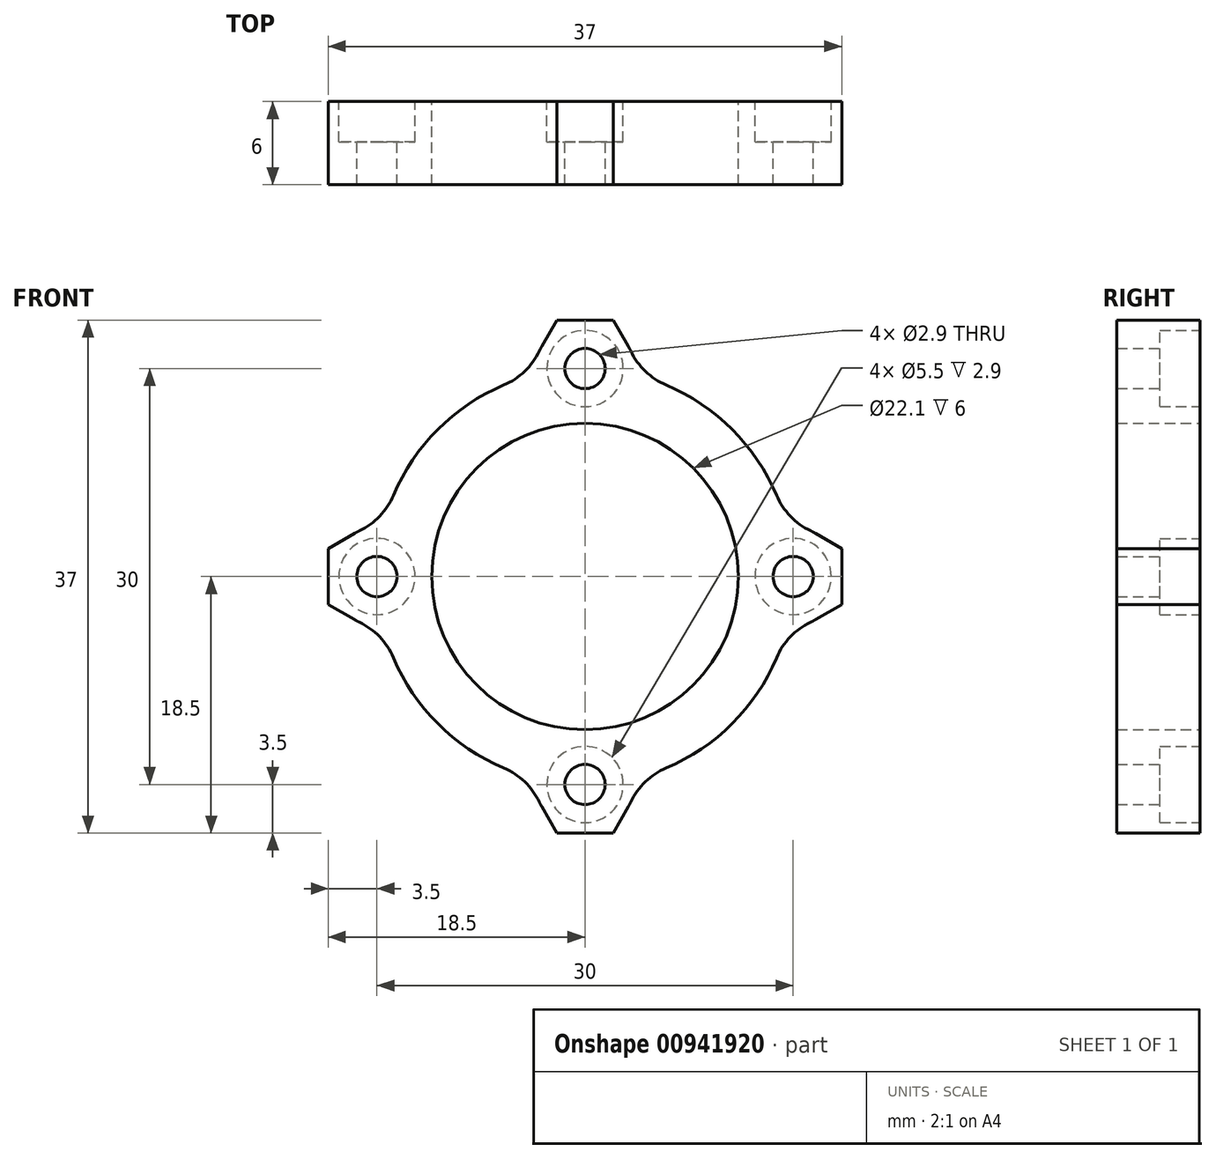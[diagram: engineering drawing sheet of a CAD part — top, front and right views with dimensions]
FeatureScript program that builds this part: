
annotation { "Feature Type Name" : "Feature", "Feature Type Description" : "" }
export const myFeature = defineFeature(function(context is Context, id is Id, definition is map)
    precondition{}
    {
        {
            var Q0;
            Q0=qCreatedBy(makeId("Front.planeOp"),FACE);
            var sketch = newSketch(context, id + "F0", { "sketchPlane" : qUnion([Q0])});
            skCircle(sketch, "E0", {"center": v(0, 0) * mm, "radius": 11.05 * mm});
            skCircle(sketch, "E1", {"center": v(0, 0) * mm, "radius": 15 * mm});
            skPoint(sketch, "E2", {"position": v(0, 15) * mm});
            skCircle(sketch, "E3.cCircle", {"center": v(0, 15) * mm, "radius": 3.5 * mm, "construction": true});
            skLineSegment(sketch, "E3.0", {"start": v(-2.02, 18.5) * mm, "end": v(2.02, 18.5) * mm});
            skLineSegment(sketch, "E3.1", {"start": v(2.02, 18.5) * mm, "end": v(4.04, 15) * mm});
            skLineSegment(sketch, "E3.2", {"start": v(4.04, 15) * mm, "end": v(2.02, 11.5) * mm});
            skLineSegment(sketch, "E3.3", {"start": v(2.02, 11.5) * mm, "end": v(-2.02, 11.5) * mm});
            skLineSegment(sketch, "E3.4", {"start": v(-2.02, 11.5) * mm, "end": v(-4.04, 15) * mm});
            skLineSegment(sketch, "E3.5", {"start": v(-4.04, 15) * mm, "end": v(-2.02, 18.5) * mm});
            skPoint(sketch, "E3.0.midPoint", {"position": v(0, 18.5) * mm});
            skPoint(sketch, "E4", {"position": v(-15, 0) * mm});
            skPoint(sketch, "E5", {"position": v(15, 0) * mm});
            skLineSegment(sketch, "E6", {"start": v(-15, 0) * mm, "end": v(15, 0) * mm});
            skLineSegment(sketch, "E7.MirrorCS", {"start": v(-2.02, -18.5) * mm, "end": v(2.02, -18.5) * mm});
            skLineSegment(sketch, "E8.MirrorCS", {"start": v(-4.04, -15) * mm, "end": v(-2.02, -18.5) * mm});
            skLineSegment(sketch, "E9.MirrorCS", {"start": v(4.04, -15) * mm, "end": v(2.02, -11.5) * mm});
            skLineSegment(sketch, "E10.MirrorCS", {"start": v(-2.02, -11.5) * mm, "end": v(-4.04, -15) * mm});
            skLineSegment(sketch, "E11.MirrorCS", {"start": v(2.02, -11.5) * mm, "end": v(-2.02, -11.5) * mm});
            skLineSegment(sketch, "E12.MirrorCS", {"start": v(2.02, -18.5) * mm, "end": v(4.04, -15) * mm});
            skLineSegment(sketch, "E13", {"start": v(0, 0) * mm, "end": v(10.6, 10.6) * mm});
            skLineSegment(sketch, "E14.MirrorCS", {"start": v(15, 4.04) * mm, "end": v(11.5, 2.02) * mm});
            skLineSegment(sketch, "E15.MirrorCS", {"start": v(11.5, 2.02) * mm, "end": v(11.5, -2.02) * mm});
            skLineSegment(sketch, "E16.MirrorCS", {"start": v(11.5, -2.02) * mm, "end": v(15, -4.04) * mm});
            skLineSegment(sketch, "E17.MirrorCS", {"start": v(15, -4.04) * mm, "end": v(18.5, -2.02) * mm});
            skLineSegment(sketch, "E18.MirrorCS", {"start": v(18.5, -2.02) * mm, "end": v(18.5, 2.02) * mm});
            skLineSegment(sketch, "E19.MirrorCS", {"start": v(18.5, 2.02) * mm, "end": v(15, 4.04) * mm});
            skLineSegment(sketch, "E20", {"start": v(0, 15) * mm, "end": v(0, 0) * mm});
            skLineSegment(sketch, "E21.MirrorCS", {"start": v(-15, 4.04) * mm, "end": v(-11.5, 2.02) * mm});
            skLineSegment(sketch, "E22.MirrorCS", {"start": v(-11.5, 2.02) * mm, "end": v(-11.5, -2.02) * mm});
            skLineSegment(sketch, "E23.MirrorCS", {"start": v(-11.5, -2.02) * mm, "end": v(-15, -4.04) * mm});
            skLineSegment(sketch, "E24.MirrorCS", {"start": v(-15, -4.04) * mm, "end": v(-18.5, -2.02) * mm});
            skLineSegment(sketch, "E25.MirrorCS", {"start": v(-18.5, -2.02) * mm, "end": v(-18.5, 2.02) * mm});
            skLineSegment(sketch, "E26.MirrorCS", {"start": v(-18.5, 2.02) * mm, "end": v(-15, 4.04) * mm});
            skCircle(sketch, "E27", {"center": v(0, 15) * mm, "radius": 1.45 * mm});
            skCircle(sketch, "E28", {"center": v(15, 0) * mm, "radius": 1.45 * mm});
            skCircle(sketch, "E29", {"center": v(-15, 0) * mm, "radius": 1.45 * mm});
            skCircle(sketch, "E30", {"center": v(0, -15) * mm, "radius": 1.45 * mm});
            skSolve(sketch);
        }
        {
            var Q0;
            Q0 = qSketchRegion(id + "F0", true);
            extrude(context, id + "F1", {"entities" : qUnion([Q0]), "depth" : 6 * mm, "offsetDistance" : 25 * mm});
        }
        {
            var Q0;
            Q0=makeQuery(id+"F1.opExtrude","SWEPT_EDGE",EDGE,{"disambiguationData":[OSD([sQuery(id+"F0.wireOp",EDGE,"E3.4"),sQuery(id+"F0.wireOp",EDGE,"E3.5")])]});
            fillet(context, id + "F2", {"entities" : qUnion([Q0]), "radius" : 5 * mm, "tangentPropagation" : true, "allowEdgeOverflow" : false});
        }
        {
            var Q0;
            {var subQ0=sQuery(id+"F0.wireOp",EDGE,"E3.4");var subQ1=sQuery(id+"F0.wireOp",EDGE,"E1");Q0=makeQuery(id+"F2.opFillet","BLEND_EDGE",EDGE,{"blendedFrom":[makeQuery(id+"F1.opExtrude","SWEPT_EDGE",EDGE,{"disambiguationData":[OSD([subQ0,sQuery(id+"F0.wireOp",EDGE,"E3.5")])]}),makeQuery(id+"F1.opExtrude","SWEPT_FACE",FACE,{"disambiguationData":[OSD([subQ1]),TDD([makeQuery(id+"F0.imprint","IMPRINT",EDGE,{"disambiguationData":[TD([[makeQuery(id+"F0.imprint","INTERSECT",VERTEX,{"derivedFrom":[subQ1,subQ0]}),-1.0]])],"derivedFrom":subQ1})])]})],"blendedInto":[makeQuery(id+"F1.opExtrude","SWEPT_FACE",FACE,{"disambiguationData":[OSD([subQ1]),TDD([makeQuery(id+"F0.imprint","IMPRINT",EDGE,{"disambiguationData":[TD([[makeQuery(id+"F0.imprint","INTERSECT",VERTEX,{"derivedFrom":[subQ1,subQ0]}),-1.0]])],"derivedFrom":subQ1})])]})]});}
            fillet(context, id + "F3", {"entities" : qUnion([Q0]), "radius" : 5 * mm, "tangentPropagation" : true, "allowEdgeOverflow" : false});
        }
        {
            var Q0;
            Q0=makeQuery(id+"F1.opExtrude","SWEPT_EDGE",EDGE,{"disambiguationData":[OSD([sQuery(id+"F0.wireOp",EDGE,"E3.1"),sQuery(id+"F0.wireOp",EDGE,"E3.2")])]});
            fillet(context, id + "F4", {"entities" : qUnion([Q0]), "radius" : 5 * mm, "tangentPropagation" : true, "allowEdgeOverflow" : false});
        }
        {
            var Q0;
            {var subQ0=sQuery(id+"F0.wireOp",EDGE,"E1");var subQ1=makeQuery(id+"F0.imprint","INTERSECT",VERTEX,{"derivedFrom":[subQ0,sQuery(id+"F0.wireOp",EDGE,"E13")]});var subQ2=sQuery(id+"F0.wireOp",EDGE,"E3.2");Q0=makeQuery(id+"F4.opFillet","BLEND_EDGE",EDGE,{"blendedFrom":[makeQuery(id+"F1.opExtrude","SWEPT_EDGE",EDGE,{"disambiguationData":[OSD([sQuery(id+"F0.wireOp",EDGE,"E3.1"),subQ2])]}),makeQuery(id+"F1.opExtrude","SWEPT_FACE",FACE,{"disambiguationData":[OSD([subQ0]),TDD([makeQuery(id+"F0.imprint","IMPRINT",EDGE,{"disambiguationData":[TD([[subQ1,1.0]])],"derivedFrom":subQ0}),makeQuery(id+"F0.imprint","IMPRINT",EDGE,{"disambiguationData":[TD([[subQ1,-1.0]])],"derivedFrom":subQ0})])]})],"blendedInto":[makeQuery(id+"F1.opExtrude","SWEPT_FACE",FACE,{"disambiguationData":[OSD([subQ0]),TDD([makeQuery(id+"F0.imprint","IMPRINT",EDGE,{"disambiguationData":[TD([[subQ1,1.0]])],"derivedFrom":subQ0}),makeQuery(id+"F0.imprint","IMPRINT",EDGE,{"disambiguationData":[TD([[subQ1,-1.0]])],"derivedFrom":subQ0})])]})]});}
            fillet(context, id + "F5", {"entities" : qUnion([Q0]), "radius" : 5 * mm, "tangentPropagation" : true, "allowEdgeOverflow" : false});
        }
        {
            var Q0;
            Q0=makeQuery(id+"F1.opExtrude","SWEPT_EDGE",EDGE,{"disambiguationData":[OSD([sQuery(id+"F0.wireOp",EDGE,"E14.MirrorCS"),sQuery(id+"F0.wireOp",EDGE,"E19.MirrorCS")])]});
            var Q1;
            Q1=makeQuery(id+"F1.opExtrude","SWEPT_EDGE",EDGE,{"disambiguationData":[OSD([sQuery(id+"F0.wireOp",EDGE,"E16.MirrorCS"),sQuery(id+"F0.wireOp",EDGE,"E17.MirrorCS")])]});
            fillet(context, id + "F6", {"entities" : qUnion([Q0, Q1]), "radius" : 5 * mm, "tangentPropagation" : true, "allowEdgeOverflow" : false});
        }
        {
            var Q0;
            {var subQ0=sQuery(id+"F0.wireOp",EDGE,"E1");var subQ1=makeQuery(id+"F0.imprint","INTERSECT",VERTEX,{"derivedFrom":[subQ0,sQuery(id+"F0.wireOp",EDGE,"E13")]});var subQ2=sQuery(id+"F0.wireOp",EDGE,"E14.MirrorCS");Q0=makeQuery(id+"F6.opFillet","BLEND_EDGE",EDGE,{"blendedFrom":[makeQuery(id+"F1.opExtrude","SWEPT_EDGE",EDGE,{"disambiguationData":[OSD([subQ2,sQuery(id+"F0.wireOp",EDGE,"E19.MirrorCS")])]}),makeQuery(id+"F1.opExtrude","SWEPT_FACE",FACE,{"disambiguationData":[OSD([subQ0]),TDD([makeQuery(id+"F0.imprint","IMPRINT",EDGE,{"disambiguationData":[TD([[subQ1,1.0]])],"derivedFrom":subQ0}),makeQuery(id+"F0.imprint","IMPRINT",EDGE,{"disambiguationData":[TD([[subQ1,-1.0]])],"derivedFrom":subQ0})])]})],"blendedInto":[makeQuery(id+"F1.opExtrude","SWEPT_FACE",FACE,{"disambiguationData":[OSD([subQ0]),TDD([makeQuery(id+"F0.imprint","IMPRINT",EDGE,{"disambiguationData":[TD([[subQ1,1.0]])],"derivedFrom":subQ0}),makeQuery(id+"F0.imprint","IMPRINT",EDGE,{"disambiguationData":[TD([[subQ1,-1.0]])],"derivedFrom":subQ0})])]})]});}
            var Q1;
            {var subQ0=sQuery(id+"F0.wireOp",EDGE,"E1");var subQ1=sQuery(id+"F0.wireOp",EDGE,"E16.MirrorCS");Q1=makeQuery(id+"F6.opFillet","BLEND_EDGE",EDGE,{"blendedFrom":[makeQuery(id+"F1.opExtrude","SWEPT_EDGE",EDGE,{"disambiguationData":[OSD([subQ1,sQuery(id+"F0.wireOp",EDGE,"E17.MirrorCS")])]}),makeQuery(id+"F1.opExtrude","SWEPT_FACE",FACE,{"disambiguationData":[OSD([subQ0]),TDD([makeQuery(id+"F0.imprint","IMPRINT",EDGE,{"disambiguationData":[TD([[makeQuery(id+"F0.imprint","INTERSECT",VERTEX,{"derivedFrom":[subQ0,sQuery(id+"F0.wireOp",EDGE,"E9.MirrorCS")]}),-1.0]])],"derivedFrom":subQ0})])]})],"blendedInto":[makeQuery(id+"F1.opExtrude","SWEPT_FACE",FACE,{"disambiguationData":[OSD([subQ0]),TDD([makeQuery(id+"F0.imprint","IMPRINT",EDGE,{"disambiguationData":[TD([[makeQuery(id+"F0.imprint","INTERSECT",VERTEX,{"derivedFrom":[subQ0,sQuery(id+"F0.wireOp",EDGE,"E9.MirrorCS")]}),-1.0]])],"derivedFrom":subQ0})])]})]});}
            fillet(context, id + "F7", {"entities" : qUnion([Q0, Q1]), "radius" : 5 * mm, "tangentPropagation" : true, "allowEdgeOverflow" : false});
        }
        {
            var Q0;
            Q0=makeQuery(id+"F1.opExtrude","SWEPT_EDGE",EDGE,{"disambiguationData":[OSD([sQuery(id+"F0.wireOp",EDGE,"E8.MirrorCS"),sQuery(id+"F0.wireOp",EDGE,"E10.MirrorCS")])]});
            fillet(context, id + "F8", {"entities" : qUnion([Q0]), "radius" : 5 * mm, "tangentPropagation" : true, "allowEdgeOverflow" : false});
        }
        {
            var Q0;
            {var subQ0=sQuery(id+"F0.wireOp",EDGE,"E1");var subQ1=sQuery(id+"F0.wireOp",EDGE,"E10.MirrorCS");Q0=makeQuery(id+"F8.opFillet","BLEND_EDGE",EDGE,{"blendedFrom":[makeQuery(id+"F1.opExtrude","SWEPT_EDGE",EDGE,{"disambiguationData":[OSD([sQuery(id+"F0.wireOp",EDGE,"E8.MirrorCS"),subQ1])]}),makeQuery(id+"F1.opExtrude","SWEPT_FACE",FACE,{"disambiguationData":[OSD([subQ0]),TDD([makeQuery(id+"F0.imprint","IMPRINT",EDGE,{"disambiguationData":[TD([[makeQuery(id+"F0.imprint","INTERSECT",VERTEX,{"derivedFrom":[subQ0,sQuery(id+"F0.wireOp",EDGE,"E23.MirrorCS")]}),-1.0]])],"derivedFrom":subQ0})])]})],"blendedInto":[makeQuery(id+"F1.opExtrude","SWEPT_FACE",FACE,{"disambiguationData":[OSD([subQ0]),TDD([makeQuery(id+"F0.imprint","IMPRINT",EDGE,{"disambiguationData":[TD([[makeQuery(id+"F0.imprint","INTERSECT",VERTEX,{"derivedFrom":[subQ0,sQuery(id+"F0.wireOp",EDGE,"E23.MirrorCS")]}),-1.0]])],"derivedFrom":subQ0})])]})]});}
            fillet(context, id + "F9", {"entities" : qUnion([Q0]), "radius" : 5 * mm, "tangentPropagation" : true, "allowEdgeOverflow" : false});
        }
        {
            var Q0;
            Q0=makeQuery(id+"F1.opExtrude","SWEPT_EDGE",EDGE,{"disambiguationData":[OSD([sQuery(id+"F0.wireOp",EDGE,"E9.MirrorCS"),sQuery(id+"F0.wireOp",EDGE,"E12.MirrorCS")])]});
            fillet(context, id + "F10", {"entities" : qUnion([Q0]), "radius" : 5 * mm, "tangentPropagation" : true, "allowEdgeOverflow" : false});
        }
        {
            var Q0;
            {var subQ0=sQuery(id+"F0.wireOp",EDGE,"E9.MirrorCS");var subQ1=sQuery(id+"F0.wireOp",EDGE,"E1");Q0=makeQuery(id+"F10.opFillet","BLEND_EDGE",EDGE,{"blendedFrom":[makeQuery(id+"F1.opExtrude","SWEPT_EDGE",EDGE,{"disambiguationData":[OSD([subQ0,sQuery(id+"F0.wireOp",EDGE,"E12.MirrorCS")])]}),makeQuery(id+"F1.opExtrude","SWEPT_FACE",FACE,{"disambiguationData":[OSD([subQ1]),TDD([makeQuery(id+"F0.imprint","IMPRINT",EDGE,{"disambiguationData":[TD([[makeQuery(id+"F0.imprint","INTERSECT",VERTEX,{"derivedFrom":[subQ1,subQ0]}),-1.0]])],"derivedFrom":subQ1})])]})],"blendedInto":[makeQuery(id+"F1.opExtrude","SWEPT_FACE",FACE,{"disambiguationData":[OSD([subQ1]),TDD([makeQuery(id+"F0.imprint","IMPRINT",EDGE,{"disambiguationData":[TD([[makeQuery(id+"F0.imprint","INTERSECT",VERTEX,{"derivedFrom":[subQ1,subQ0]}),-1.0]])],"derivedFrom":subQ1})])]})]});}
            fillet(context, id + "F11", {"entities" : qUnion([Q0]), "radius" : 5 * mm, "tangentPropagation" : true, "allowEdgeOverflow" : false});
        }
        {
            var Q0;
            Q0=makeQuery(id+"F1.opExtrude","SWEPT_EDGE",EDGE,{"disambiguationData":[OSD([sQuery(id+"F0.wireOp",EDGE,"E23.MirrorCS"),sQuery(id+"F0.wireOp",EDGE,"E24.MirrorCS")])]});
            var Q1;
            Q1=makeQuery(id+"F1.opExtrude","SWEPT_EDGE",EDGE,{"disambiguationData":[OSD([sQuery(id+"F0.wireOp",EDGE,"E21.MirrorCS"),sQuery(id+"F0.wireOp",EDGE,"E26.MirrorCS")])]});
            fillet(context, id + "F12", {"entities" : qUnion([Q0, Q1]), "radius" : 5 * mm, "tangentPropagation" : true, "allowEdgeOverflow" : false});
        }
        {
            var Q0;
            {var subQ0=sQuery(id+"F0.wireOp",EDGE,"E1");var subQ1=sQuery(id+"F0.wireOp",EDGE,"E21.MirrorCS");Q0=makeQuery(id+"F12.opFillet","BLEND_EDGE",EDGE,{"blendedFrom":[makeQuery(id+"F1.opExtrude","SWEPT_EDGE",EDGE,{"disambiguationData":[OSD([subQ1,sQuery(id+"F0.wireOp",EDGE,"E26.MirrorCS")])]}),makeQuery(id+"F1.opExtrude","SWEPT_FACE",FACE,{"disambiguationData":[OSD([subQ0]),TDD([makeQuery(id+"F0.imprint","IMPRINT",EDGE,{"disambiguationData":[TD([[makeQuery(id+"F0.imprint","INTERSECT",VERTEX,{"derivedFrom":[subQ0,sQuery(id+"F0.wireOp",EDGE,"E3.4")]}),-1.0]])],"derivedFrom":subQ0})])]})],"blendedInto":[makeQuery(id+"F1.opExtrude","SWEPT_FACE",FACE,{"disambiguationData":[OSD([subQ0]),TDD([makeQuery(id+"F0.imprint","IMPRINT",EDGE,{"disambiguationData":[TD([[makeQuery(id+"F0.imprint","INTERSECT",VERTEX,{"derivedFrom":[subQ0,sQuery(id+"F0.wireOp",EDGE,"E3.4")]}),-1.0]])],"derivedFrom":subQ0})])]})]});}
            var Q1;
            {var subQ0=sQuery(id+"F0.wireOp",EDGE,"E23.MirrorCS");var subQ1=sQuery(id+"F0.wireOp",EDGE,"E1");Q1=makeQuery(id+"F12.opFillet","BLEND_EDGE",EDGE,{"blendedFrom":[makeQuery(id+"F1.opExtrude","SWEPT_EDGE",EDGE,{"disambiguationData":[OSD([subQ0,sQuery(id+"F0.wireOp",EDGE,"E24.MirrorCS")])]}),makeQuery(id+"F1.opExtrude","SWEPT_FACE",FACE,{"disambiguationData":[OSD([subQ1]),TDD([makeQuery(id+"F0.imprint","IMPRINT",EDGE,{"disambiguationData":[TD([[makeQuery(id+"F0.imprint","INTERSECT",VERTEX,{"derivedFrom":[subQ1,subQ0]}),-1.0]])],"derivedFrom":subQ1})])]})],"blendedInto":[makeQuery(id+"F1.opExtrude","SWEPT_FACE",FACE,{"disambiguationData":[OSD([subQ1]),TDD([makeQuery(id+"F0.imprint","IMPRINT",EDGE,{"disambiguationData":[TD([[makeQuery(id+"F0.imprint","INTERSECT",VERTEX,{"derivedFrom":[subQ1,subQ0]}),-1.0]])],"derivedFrom":subQ1})])]})]});}
            fillet(context, id + "F13", {"entities" : qUnion([Q0, Q1]), "radius" : 5 * mm, "tangentPropagation" : true, "allowEdgeOverflow" : false});
        }
        {
            var Q0;
            Q0=qCreatedBy(makeId("Front.planeOp"),FACE);
            var sketch = newSketch(context, id + "F14", { "sketchPlane" : qUnion([Q0])});
            skCircle(sketch, "E31", {"center": v(0, 15) * mm, "radius": 2.75 * mm});
            skCircle(sketch, "E32.MirrorC", {"center": v(0, -15) * mm, "radius": 2.75 * mm});
            skCircle(sketch, "E33.MirrorC", {"center": v(15, 0) * mm, "radius": 2.75 * mm});
            skCircle(sketch, "E34.MirrorC", {"center": v(-15, 0) * mm, "radius": 2.75 * mm});
            skSolve(sketch);
        }
        {
            var Q0;
            Q0 = qSketchRegion(id + "F14", true);
            extrude(context, id + "F15", {"entities" : qUnion([Q0]), "operationType" : NewBodyOperationType.REMOVE, "depth" : 2.9 * mm, "offsetDistance" : 25 * mm});
        }
    });
